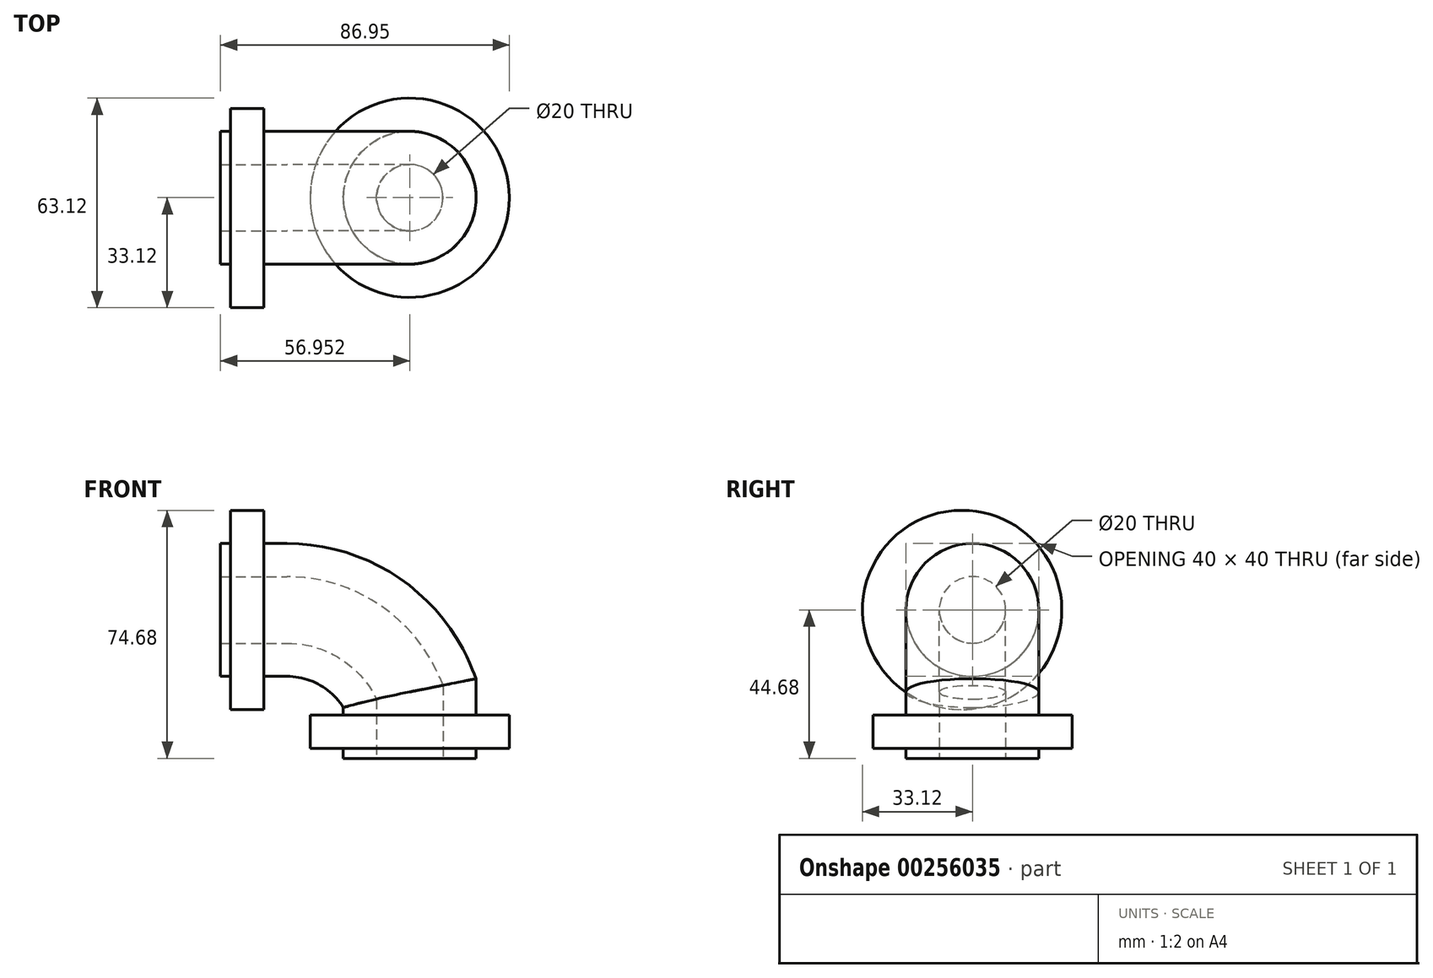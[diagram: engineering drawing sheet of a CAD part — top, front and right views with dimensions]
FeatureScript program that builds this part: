
annotation { "Feature Type Name" : "Feature", "Feature Type Description" : "" }
export const myFeature = defineFeature(function(context is Context, id is Id, definition is map)
    precondition{}
    {
        {
            var Q0;
            Q0=qCreatedBy(makeId("Right.planeOp"),FACE);
            var sketch = newSketch(context, id + "F0", { "sketchPlane" : qUnion([Q0])});
            skCircle(sketch, "E0", {"center": v(0, 0) * mm, "radius": 10 * mm});
            skCircle(sketch, "E1", {"center": v(0, 0) * mm, "radius": 20 * mm});
            skSolve(sketch);
        }
        {
            var Q0;
            Q0=qCreatedBy(makeId("Front.planeOp"),FACE);
            var sketch = newSketch(context, id + "F1", { "sketchPlane" : qUnion([Q0])});
            skLineSegment(sketch, "E2", {"start": v(0, 0) * mm, "end": v(20, 0) * mm});
            skArc(sketch, "E3", {"start": v(20, 0) * mm, "mid": v(42.22, -6.74) * mm, "end": v(56.95, -24.68) * mm});
            skLineSegment(sketch, "E4", {"start": v(56.95, -24.68) * mm, "end": v(56.95, -44.68) * mm});
            skSolve(sketch);
        }
        {
            var Q0;
            Q0=makeQuery(id+"F0.imprint","IMPRINT",FACE,{"disambiguationData":[TD([[makeQuery(id+"F0.imprint","IMPRINT",EDGE,{"derivedFrom":sQuery(id+"F0.wireOp",EDGE,"E0")}),-1.0]])]});
            var Q1;
            Q1=sQuery(id+"F1.wireOp",EDGE,"E2");
            var Q2;
            Q2=sQuery(id+"F1.wireOp",EDGE,"E3");
            var Q3;
            Q3=sQuery(id+"F1.wireOp",EDGE,"E4");
            sweep(context, id + "F2", {"profiles" : qUnion([Q0]), "path" : qUnion([Q1, Q2, Q3])});
        }
        {
            var Q0;
            Q0=makeQuery(id+"F2.opSweep","CAP_FACE",FACE,{"disambiguationData":[OSD([sQuery(id+"F0.wireOp",EDGE,"E0"),sQuery(id+"F0.wireOp",EDGE,"E1"),sQuery(id+"F1.wireOp",VERTEX,"E2.start")])],"isStart":true});
            cPlane(context, id + "F3", {"entities" : qUnion([Q0]), "cplaneType" : CPlaneType.OFFSET, "offset" : 3 * mm, "oppositeDirection" : true, "width" : 150 * mm, "height" : 150 * mm});
        }
        {
            var Q0;
            Q0=qCreatedBy(id+"F3.planeOp",FACE);
            var sketch = newSketch(context, id + "F4", { "sketchPlane" : qUnion([Q0])});
            skCircle(sketch, "E5", {"center": v(3.12, 0) * mm, "radius": 30 * mm});
            skCircle(sketch, "E6.0", {"center": v(0, 0) * mm, "radius": 20 * mm});
            skSolve(sketch);
        }
        {
            var Q0;
            Q0=makeQuery(id+"F4.imprint","IMPRINT",FACE,{"disambiguationData":[TD([[makeQuery(id+"F4.imprint","IMPRINT",EDGE,{"derivedFrom":sQuery(id+"F4.wireOp",EDGE,"E5")}),1.0]])]});
            extrude(context, id + "F5", {"entities" : qUnion([Q0]), "operationType" : NewBodyOperationType.ADD, "oppositeDirection" : true, "depth" : 10 * mm});
        }
        {
            var Q0;
            Q0=makeQuery(id+"F2.opSweep","CAP_FACE",FACE,{"disambiguationData":[OSD([sQuery(id+"F0.wireOp",EDGE,"E0"),sQuery(id+"F0.wireOp",EDGE,"E1"),sQuery(id+"F1.wireOp",VERTEX,"E4.end")])],"isStart":false});
            cPlane(context, id + "F6", {"entities" : qUnion([Q0]), "cplaneType" : CPlaneType.OFFSET, "offset" : 3 * mm, "oppositeDirection" : true, "width" : 150 * mm, "height" : 150 * mm});
        }
        {
            var Q0;
            Q0=qCreatedBy(id+"F6.planeOp",FACE);
            var sketch = newSketch(context, id + "F7", { "sketchPlane" : qUnion([Q0])});
            skCircle(sketch, "E7.0", {"center": v(56.95, 0) * mm, "radius": 20 * mm});
            skCircle(sketch, "E8", {"center": v(56.95, 0) * mm, "radius": 30 * mm});
            skSolve(sketch);
        }
        {
            var Q0;
            Q0=makeQuery(id+"F7.imprint","IMPRINT",FACE,{"disambiguationData":[TD([[makeQuery(id+"F7.imprint","IMPRINT",EDGE,{"derivedFrom":sQuery(id+"F7.wireOp",EDGE,"E7.0")}),-1.0]])]});
            extrude(context, id + "F8", {"entities" : qUnion([Q0]), "operationType" : NewBodyOperationType.ADD, "oppositeDirection" : true, "depth" : 10 * mm});
        }
    });
